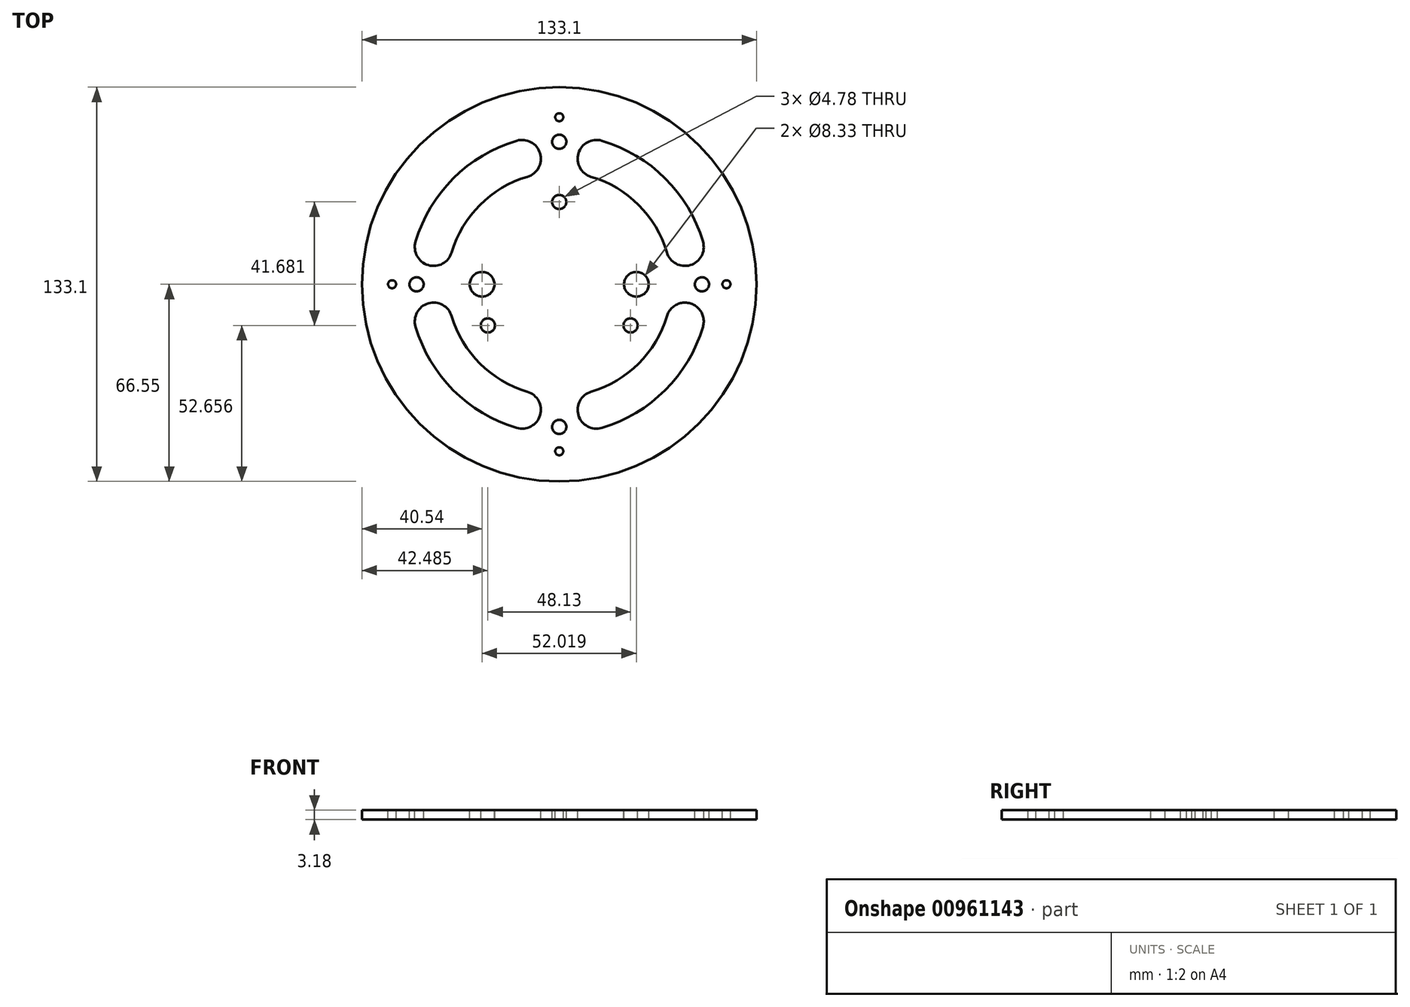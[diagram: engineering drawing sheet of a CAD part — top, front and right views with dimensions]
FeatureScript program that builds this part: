
annotation { "Feature Type Name" : "Feature", "Feature Type Description" : "" }
export const myFeature = defineFeature(function(context is Context, id is Id, definition is map)
    precondition{}
    {
        {
            var Q0;
            Q0=qCreatedBy(makeId("Top.planeOp"),FACE);
            var sketch = newSketch(context, id + "F0", { "sketchPlane" : qUnion([Q0])});
            skCircle(sketch, "E0", {"center": v(0, 0) * mm, "radius": 66.55 * mm});
            skCircle(sketch, "E1", {"center": v(0, 27.79) * mm, "radius": 2.39 * mm});
            skCircle(sketch, "E2", {"center": v(24.06, -13.9) * mm, "radius": 2.39 * mm});
            skCircle(sketch, "E3", {"center": v(-24.06, -13.9) * mm, "radius": 2.39 * mm});
            skCircle(sketch, "E4", {"center": v(-26, 0) * mm, "radius": 4.17 * mm});
            skCircle(sketch, "E5", {"center": v(26, 0) * mm, "radius": 4.17 * mm});
            skPoint(sketch, "E6.orphan", {"position": v(0, 66.55) * mm});
            skSolve(sketch);
        }
        {
            var Q0;
            Q0=qCreatedBy(makeId("Top.planeOp"),FACE);
            var sketch = newSketch(context, id + "F1", { "sketchPlane" : qUnion([Q0])});
            skArc(sketch, "E7", {"start": v(14.35, 48.47) * mm, "mid": v(6.46, 44.18) * mm, "end": v(10.74, 36.29) * mm});
            skArc(sketch, "E8", {"start": v(36.29, 10.74) * mm, "mid": v(44.18, 6.46) * mm, "end": v(48.47, 14.35) * mm});
            skArc(sketch, "E9", {"start": v(48.47, -14.35) * mm, "mid": v(44.18, -6.46) * mm, "end": v(36.29, -10.74) * mm});
            skArc(sketch, "E10", {"start": v(10.74, -36.29) * mm, "mid": v(6.46, -44.18) * mm, "end": v(14.35, -48.47) * mm});
            skArc(sketch, "E11", {"start": v(-14.35, -48.47) * mm, "mid": v(-6.46, -44.18) * mm, "end": v(-10.74, -36.29) * mm});
            skArc(sketch, "E12", {"start": v(-36.29, -10.74) * mm, "mid": v(-44.18, -6.46) * mm, "end": v(-48.47, -14.35) * mm});
            skArc(sketch, "E13", {"start": v(-48.47, 14.35) * mm, "mid": v(-44.18, 6.46) * mm, "end": v(-36.29, 10.74) * mm});
            skArc(sketch, "E14", {"start": v(-10.74, 36.29) * mm, "mid": v(-6.46, 44.18) * mm, "end": v(-14.35, 48.47) * mm});
            skArc(sketch, "E15", {"start": v(48.47, 14.35) * mm, "mid": v(35.74, 35.74) * mm, "end": v(14.35, 48.47) * mm});
            skArc(sketch, "E16", {"start": v(36.29, 10.74) * mm, "mid": v(26.76, 26.76) * mm, "end": v(10.74, 36.29) * mm});
            skArc(sketch, "E17.trimOffspring", {"start": v(-10.74, 36.29) * mm, "mid": v(-26.76, 26.76) * mm, "end": v(-36.29, 10.74) * mm});
            skArc(sketch, "E18.trimOffspring", {"start": v(-14.35, 48.47) * mm, "mid": v(-35.74, 35.74) * mm, "end": v(-48.47, 14.35) * mm});
            skArc(sketch, "E19.trimOffspring", {"start": v(-36.29, -10.74) * mm, "mid": v(-26.76, -26.76) * mm, "end": v(-10.74, -36.29) * mm});
            skArc(sketch, "E20.trimOffspring", {"start": v(-48.47, -14.35) * mm, "mid": v(-35.74, -35.74) * mm, "end": v(-14.35, -48.47) * mm});
            skArc(sketch, "E21.trimOffspring", {"start": v(10.74, -36.29) * mm, "mid": v(26.76, -26.76) * mm, "end": v(36.29, -10.74) * mm});
            skArc(sketch, "E22.trimOffspring", {"start": v(14.35, -48.47) * mm, "mid": v(35.74, -35.74) * mm, "end": v(48.47, -14.35) * mm});
            skPoint(sketch, "E23.start.orphan", {"position": v(-75.85, 0) * mm});
            skPoint(sketch, "E24.orphan", {"position": v(0, 76.62) * mm});
            skSolve(sketch);
        }
        {
            var Q0;
            Q0=qCreatedBy(makeId("Top.planeOp"),FACE);
            var sketch = newSketch(context, id + "F2", { "sketchPlane" : qUnion([Q0])});
            skCircle(sketch, "E25", {"center": v(0, -48.13) * mm, "radius": 2.39 * mm});
            skCircle(sketch, "E26", {"center": v(-48.13, 0) * mm, "radius": 2.39 * mm});
            skCircle(sketch, "E27", {"center": v(48.13, 0) * mm, "radius": 2.39 * mm});
            skCircle(sketch, "E28", {"center": v(0, 48.13) * mm, "radius": 2.39 * mm});
            skCircle(sketch, "E29", {"center": v(0, -56.39) * mm, "radius": 1.35 * mm});
            skCircle(sketch, "E30", {"center": v(56.39, 0) * mm, "radius": 1.35 * mm});
            skCircle(sketch, "E31", {"center": v(0, 56.39) * mm, "radius": 1.35 * mm});
            skCircle(sketch, "E32", {"center": v(-56.39, 0) * mm, "radius": 1.35 * mm});
            skSolve(sketch);
        }
        {
            var Q0;
            Q0 = qSketchRegion(id + "F0", true);
            var Q1;
            Q1 = qSketchRegion(id + "F1", true);
            var Q2;
            Q2 = qSketchRegion(id + "F2", true);
            extrude(context, id + "F3", {"entities" : qUnion([Q0, Q1, Q2]), "oppositeDirection" : true, "depth" : 3.17 * mm, "offsetDistance" : 25.4 * mm});
        }
    });
